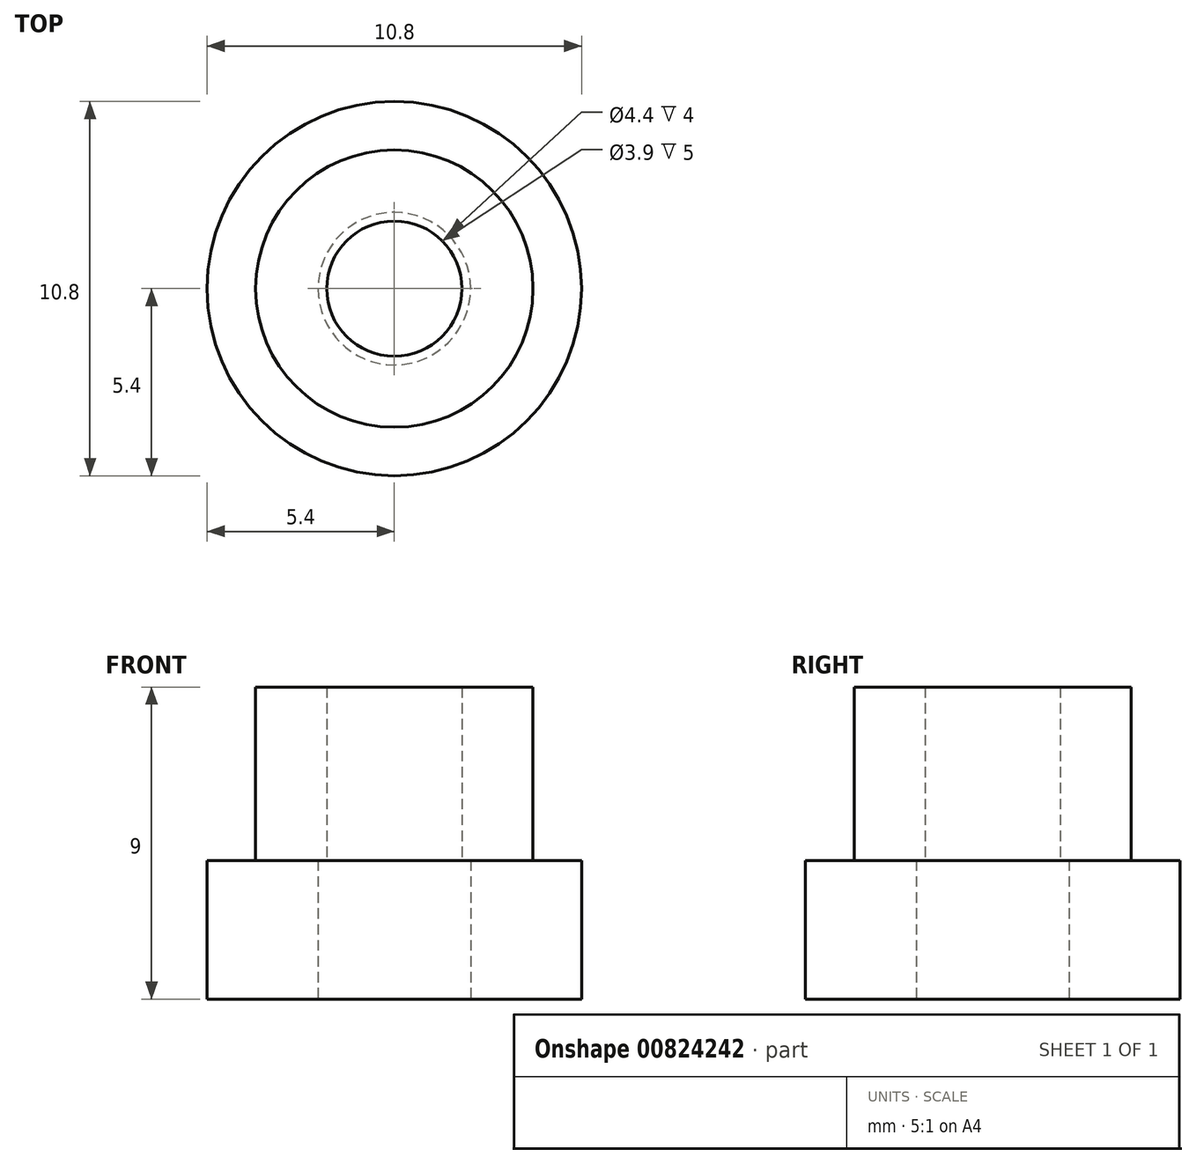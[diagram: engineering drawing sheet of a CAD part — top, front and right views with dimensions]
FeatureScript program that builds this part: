
annotation { "Feature Type Name" : "Feature", "Feature Type Description" : "" }
export const myFeature = defineFeature(function(context is Context, id is Id, definition is map)
    precondition{}
    {
        {
            var Q0;
            Q0=qCreatedBy(makeId("Top.planeOp"),FACE);
            var sketch = newSketch(context, id + "F0", { "sketchPlane" : qUnion([Q0])});
            skCircle(sketch, "E0", {"center": v(0, 0) * mm, "radius": 2.2 * mm});
            skCircle(sketch, "E1", {"center": v(0, 0) * mm, "radius": 5.4 * mm});
            skSolve(sketch);
        }
        {
            var Q0;
            Q0 = qSketchRegion(id + "F0", true);
            extrude(context, id + "F1", {"entities" : qUnion([Q0]), "depth" : 4 * mm, "offsetDistance" : 25 * mm});
        }
        {
            var Q0;
            Q0=makeQuery(id+"F1.opExtrude","CAP_FACE",FACE,{"disambiguationData":[OSD([sQuery(id+"F0.wireOp",EDGE,"E0"),sQuery(id+"F0.wireOp",EDGE,"E1")])],"isStart":false});
            var sketch = newSketch(context, id + "F2", { "sketchPlane" : qUnion([Q0])});
            skCircle(sketch, "E2", {"center": v(0, 0) * mm, "radius": 1.95 * mm});
            skCircle(sketch, "E3", {"center": v(0, 0) * mm, "radius": 4 * mm});
            skSolve(sketch);
        }
        {
            var Q0;
            Q0=makeQuery(id+"F2.imprint","IMPRINT",FACE,{"disambiguationData":[TD([[makeQuery(id+"F2.imprint","IMPRINT",EDGE,{"derivedFrom":sQuery(id+"F2.wireOp",EDGE,"E2")}),-1.0]])]});
            var Q1;
            Q1=makeQuery(id+"F2.imprint","IMPRINT",FACE,{"disambiguationData":[TD([[makeQuery(id+"F2.imprint","IMPRINT",EDGE,{"derivedFrom":makeQuery(id+"F1.opExtrude","CAP_EDGE",EDGE,{"disambiguationData":[OSD([sQuery(id+"F0.wireOp",EDGE,"E0")])],"isStart":false})}),-1.0]])]});
            extrude(context, id + "F3", {"entities" : qUnion([Q0, Q1]), "operationType" : NewBodyOperationType.ADD, "depth" : 5 * mm, "offsetDistance" : 25 * mm});
        }
    });
